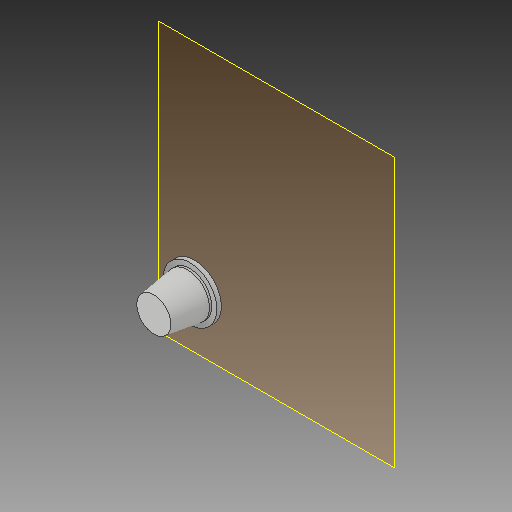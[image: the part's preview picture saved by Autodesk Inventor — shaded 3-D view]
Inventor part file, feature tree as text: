
AUTODESK INVENTOR PART (.ipt)
format: ipt  version: 2018 (Build 220112000, 112)  size: 102,400 bytes
history: native  units: mm
features: other x7, extrude x2, sketch x2, chamfer x1, plane x1, reference x1
ambient origin geometry x8: Origin, YZ Plane, XZ Plane, XY Plane, X Axis, Y Axis, Z Axis, Center Point
bodies: Solid1 (feature_tree)
feature tree (14):
  extrude  "Extrusion1"  Depth=2.0mm
  chamfer  "Chamfer2"  Distance=2.0mm
  plane  "Work Plane1"
  extrude  "Extrusion2"  [1 undecoded]
  sketch  "Sketch1"  dims[d0=18.0mm d1=0.0mm d5=15.0mm d6=2.0mm d7=1.396263mm d8=2.0mm d9=0.0mm]
  reference  "Reference1"
  sketch  "Sketch2"
  parser-record x2  (decoder bookkeeping rows leaked as tree rows — omitted from the tree; the rows remain in map.json)
  other  "LCD Mount Front.iam"
  other  "Smart-ControllerandBracket:1"
  other  "Full Graphic Smart Controller:1"
  other  "LCD-Mount.iam"
  other  "LCD-Front:1"
note: 1 required parameter value undecoded (feature->parameter linkage not recoverable at this tier; creation-order binding heuristic only, values carry confidence <= 0.55)
note: 2 file-system paths scrubbed to <path> (originals preserved in map.json)
